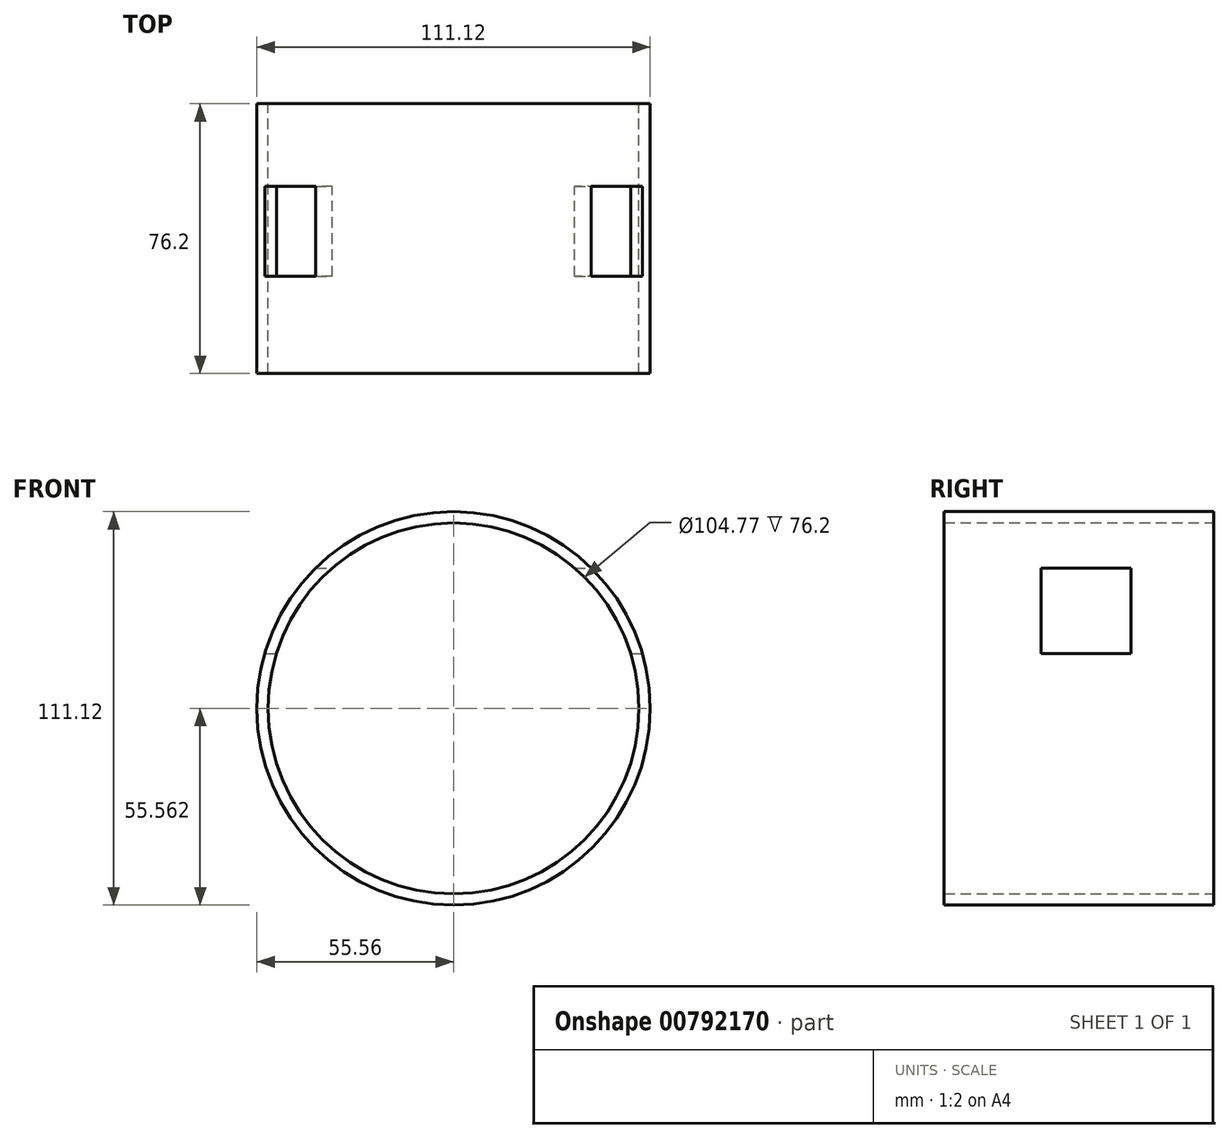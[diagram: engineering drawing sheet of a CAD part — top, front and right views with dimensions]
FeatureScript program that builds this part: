
annotation { "Feature Type Name" : "Feature", "Feature Type Description" : "" }
export const myFeature = defineFeature(function(context is Context, id is Id, definition is map)
    precondition{}
    {
        {
            var Q0;
            Q0=qCreatedBy(makeId("Front.planeOp"),FACE);
            var sketch = newSketch(context, id + "F0", { "sketchPlane" : qUnion([Q0])});
            skCircle(sketch, "E0", {"center": v(18.44, 33.41) * mm, "radius": 52.39 * mm});
            skCircle(sketch, "E1.0", {"center": v(18.44, 33.41) * mm, "radius": 55.56 * mm});
            skSolve(sketch);
        }
        {
            var Q0;
            Q0 = qSketchRegion(id + "F0", true);
            extrude(context, id + "F1", {"entities" : qUnion([Q0]), "depth" : 76.2 * mm, "offsetDistance" : 25.4 * mm});
        }
        {
            var Q0;
            Q0=qCreatedBy(makeId("Right.planeOp"),FACE);
            var sketch = newSketch(context, id + "F2", { "sketchPlane" : qUnion([Q0])});
            skLineSegment(sketch, "E2.bottom", {"start": v(-48.77, 73.09) * mm, "end": v(-23.37, 73.09) * mm});
            skLineSegment(sketch, "E2.top", {"start": v(-48.77, 48.96) * mm, "end": v(-23.37, 48.96) * mm});
            skLineSegment(sketch, "E2.left", {"start": v(-48.77, 73.09) * mm, "end": v(-48.77, 48.96) * mm});
            skLineSegment(sketch, "E2.right", {"start": v(-23.37, 73.09) * mm, "end": v(-23.37, 48.96) * mm});
            skSolve(sketch);
        }
        {
            var Q0;
            Q0 = qSketchRegion(id + "F2", true);
            extrude(context, id + "F3", {"entities" : qUnion([Q0]), "operationType" : NewBodyOperationType.REMOVE, "oppositeDirection" : true, "depth" : 76.2 * mm, "offsetDistance" : 25.4 * mm, "hasSecondDirection" : true, "secondDirectionOppositeDirection" : false, "secondDirectionDepth" : 76.2 * mm});
        }
    });
